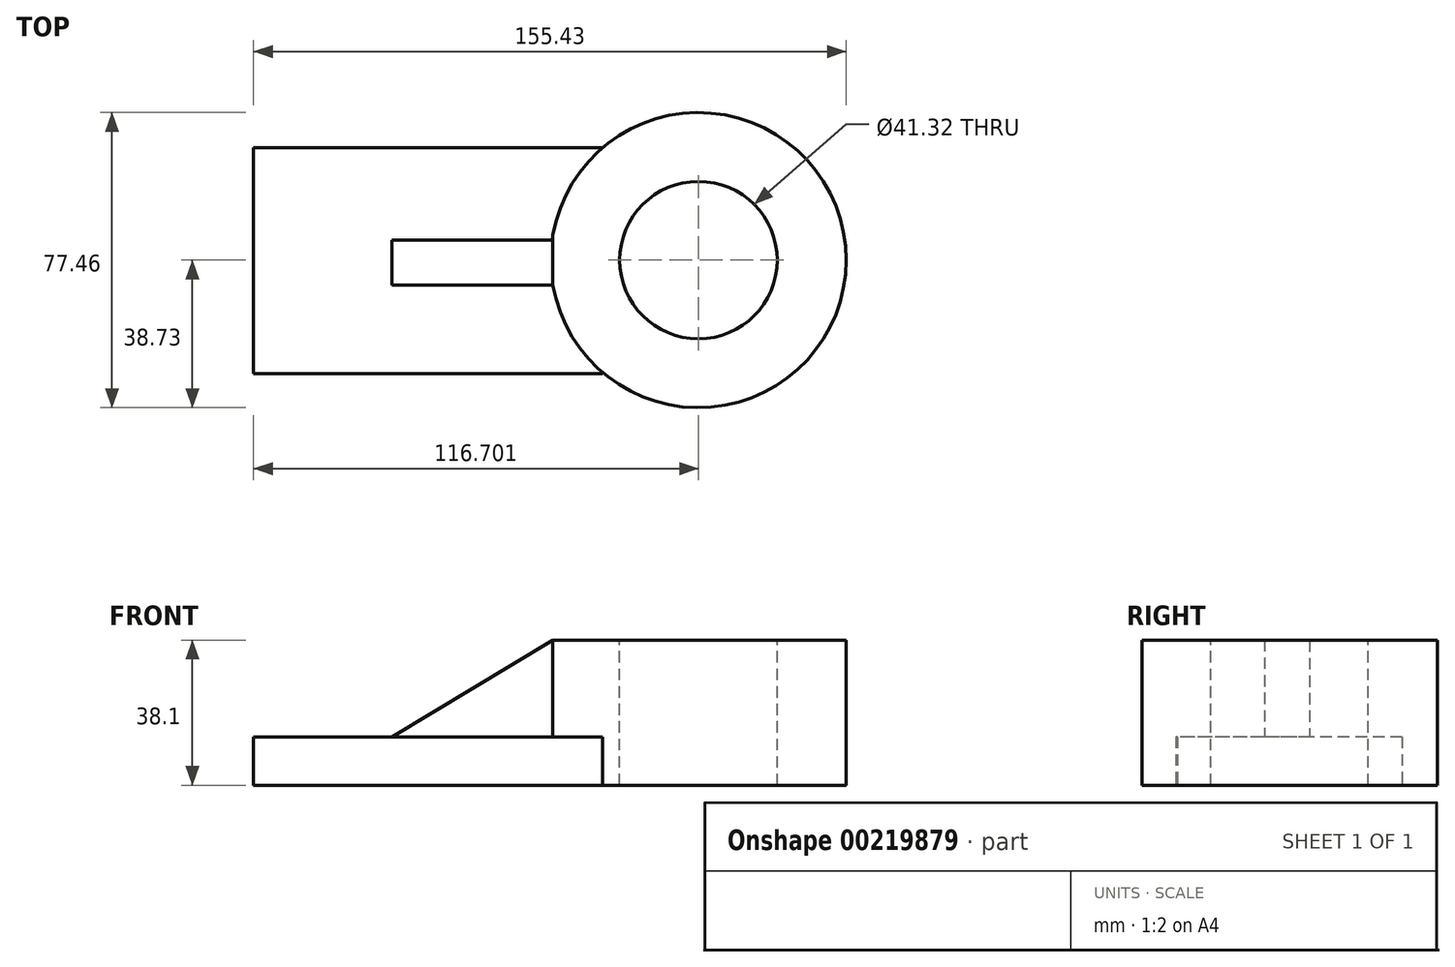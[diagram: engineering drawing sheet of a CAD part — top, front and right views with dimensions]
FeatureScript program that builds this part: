
annotation { "Feature Type Name" : "Feature", "Feature Type Description" : "" }
export const myFeature = defineFeature(function(context is Context, id is Id, definition is map)
    precondition{}
    {
        {
            var Q0;
            Q0=qCreatedBy(makeId("Top.planeOp"),FACE);
            var sketch = newSketch(context, id + "F0", { "sketchPlane" : qUnion([Q0])});
            skLineSegment(sketch, "E0.bottom", {"start": v(-52.8, 29.52) * mm, "end": v(38.76, 29.52) * mm});
            skLineSegment(sketch, "E0.top", {"start": v(-52.8, -29.8) * mm, "end": v(38.76, -29.8) * mm});
            skLineSegment(sketch, "E0.left", {"start": v(-52.8, 29.52) * mm, "end": v(-52.8, -29.8) * mm});
            skLineSegment(sketch, "E0.right", {"start": v(38.76, 29.52) * mm, "end": v(38.76, -29.8) * mm});
            skCircle(sketch, "E1", {"center": v(67.85, 0) * mm, "radius": 41.37 * mm});
            skSolve(sketch);
        }
        {
            var Q0;
            {var subQ1=sQuery(id+"F0.wireOp",EDGE,"E0.bottom");Q0=makeQuery(id+"F0.imprint","IMPRINT",FACE,{"disambiguationData":[TD([[makeQuery(id+"F0.imprint","IMPRINT",EDGE,{"derivedFrom":subQ1}),-1.0]])]});}
            var Q1;
            {var subQ0=sQuery(id+"F0.wireOp",EDGE,"E1");var subQ1=sQuery(id+"F0.wireOp",EDGE,"E0.right");var subQ2=makeQuery(id+"F0.imprint","INTERSECT",VERTEX,{"disambiguationData":[OD(0.0)],"derivedFrom":[subQ1,subQ0]});Q1=makeQuery(id+"F0.imprint","IMPRINT",FACE,{"disambiguationData":[TD([[makeQuery(id+"F0.imprint","IMPRINT",EDGE,{"disambiguationData":[TD([[subQ2,-1.0]])],"derivedFrom":subQ1}),-1.0]])]});}
            extrude(context, id + "F1", {"entities" : qUnion([Q0, Q1]), "depth" : 12.7 * mm});
        }
        {
            var Q0;
            Q0=qCreatedBy(makeId("Top.planeOp"),FACE);
            var sketch = newSketch(context, id + "F2", { "sketchPlane" : qUnion([Q0])});
            skCircle(sketch, "E2", {"center": v(63.9, 0) * mm, "radius": 38.73 * mm});
            skSolve(sketch);
        }
        {
            var Q0;
            Q0=makeQuery(id+"F2.imprint","IMPRINT",FACE,{"disambiguationData":[TD([[makeQuery(id+"F2.imprint","IMPRINT",EDGE,{"derivedFrom":sQuery(id+"F2.wireOp",EDGE,"E2")}),1.0]])]});
            extrude(context, id + "F3", {"entities" : qUnion([Q0]), "operationType" : NewBodyOperationType.ADD, "depth" : 38.1 * mm});
        }
        {
            var Q0;
            Q0=makeQuery(id+"F1.opExtrude","CAP_FACE",FACE,{"disambiguationData":[OSD([sQuery(id+"F0.wireOp",EDGE,"E0.bottom"),sQuery(id+"F0.wireOp",EDGE,"E0.top"),sQuery(id+"F0.wireOp",EDGE,"E0.left"),sQuery(id+"F0.wireOp",EDGE,"E0.right")])],"isStart":false});
            var sketch = newSketch(context, id + "F4", { "sketchPlane" : qUnion([Q0])});
            skLineSegment(sketch, "E3.bottom", {"start": v(-16.45, 5.28) * mm, "end": v(25.72, 5.28) * mm});
            skLineSegment(sketch, "E3.top", {"start": v(-16.45, -6.5) * mm, "end": v(25.72, -6.5) * mm});
            skLineSegment(sketch, "E3.left", {"start": v(-16.45, 5.28) * mm, "end": v(-16.45, -6.5) * mm});
            skLineSegment(sketch, "E3.right", {"start": v(25.72, 5.28) * mm, "end": v(25.72, -6.5) * mm});
            skSolve(sketch);
        }
        {
            var Q0;
            Q0 = qSketchRegion(id + "F4", true);
            extrude(context, id + "F5", {"entities" : qUnion([Q0]), "operationType" : NewBodyOperationType.ADD, "depth" : 25.4 * mm});
        }
        {
            var Q0;
            Q0=makeQuery(id+"F5.opExtrude","SWEPT_FACE",FACE,{"disambiguationData":[OSD([sQuery(id+"F4.wireOp",EDGE,"E3.top")])]});
            var sketch = newSketch(context, id + "F6", { "sketchPlane" : qUnion([Q0])});
            skLineSegment(sketch, "E4", {"start": v(25.72, 38.1) * mm, "end": v(-16.45, 12.7) * mm});
            skLineSegment(sketch, "E5", {"start": v(-16.45, 12.7) * mm, "end": v(-16.45, 38.1) * mm});
            skLineSegment(sketch, "E6", {"start": v(-16.45, 38.1) * mm, "end": v(25.72, 38.1) * mm});
            skSolve(sketch);
        }
        {
            var Q0;
            Q0 = qSketchRegion(id + "F6", true);
            extrude(context, id + "F7", {"entities" : qUnion([Q0]), "operationType" : NewBodyOperationType.REMOVE, "oppositeDirection" : true, "depth" : 25.4 * mm});
        }
        {
            var Q0;
            Q0=makeQuery(id+"F5.boolean.opBoolean","MERGE",FACE,{"derivedFrom":[makeQuery(id+"F3.opExtrude","CAP_FACE",FACE,{"disambiguationData":[OSD([sQuery(id+"F2.wireOp",EDGE,"E2")])],"isStart":false}),makeQuery(id+"F5.opExtrude","CAP_FACE",FACE,{"disambiguationData":[OSD([sQuery(id+"F4.wireOp",EDGE,"E3.bottom"),sQuery(id+"F4.wireOp",EDGE,"E3.top"),sQuery(id+"F4.wireOp",EDGE,"E3.left"),sQuery(id+"F4.wireOp",EDGE,"E3.right")])],"isStart":false})]});
            var sketch = newSketch(context, id + "F8", { "sketchPlane" : qUnion([Q0])});
            skCircle(sketch, "E7", {"center": v(63.9, 0) * mm, "radius": 20.66 * mm});
            skSolve(sketch);
        }
        {
            var Q0;
            Q0 = qSketchRegion(id + "F8", true);
            extrude(context, id + "F9", {"entities" : qUnion([Q0]), "operationType" : NewBodyOperationType.REMOVE, "oppositeDirection" : true, "depth" : 50.8 * mm});
        }
    });
